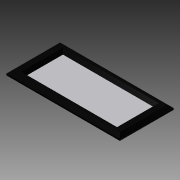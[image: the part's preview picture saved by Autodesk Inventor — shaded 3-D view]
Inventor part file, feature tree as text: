
AUTODESK INVENTOR PART (.ipt)
format: ipt  version: 2013 SP1 (Build 170176100, 176)  size: 116,224 bytes
history: native  units: mm
features: extrude x2, chamfer x2, sketch x2
ambient origin geometry x8: Origin, YZ Plane, XZ Plane, XY Plane, X Axis, Y Axis, Z Axis, Center Point
bodies: Volumenkörper1 (feature_tree), Volumenkörper2 (feature_tree)
feature tree (6):
  extrude  "Extrusion1"  Depth=36.4mm
  extrude  "Extrusion2"  Depth=24.2mm
  chamfer  "Fase1"  Distance=3.0mm
  chamfer  "Fase2"  Distance=60.8mm
  sketch  "Skizze1"  dims[d0=76.8mm d1=36.4mm]
  sketch  "Skizze2"  dims[d2=60.8mm d3=24.2mm d4=3.0mm d5=0.0mm d6=60.8mm d7=24.2mm d8=1.0mm d9=0.0mm d10=2.0mm d11=2.0mm d12=45.0deg d13=2.0mm d14=2.0mm d15=45.0deg]
